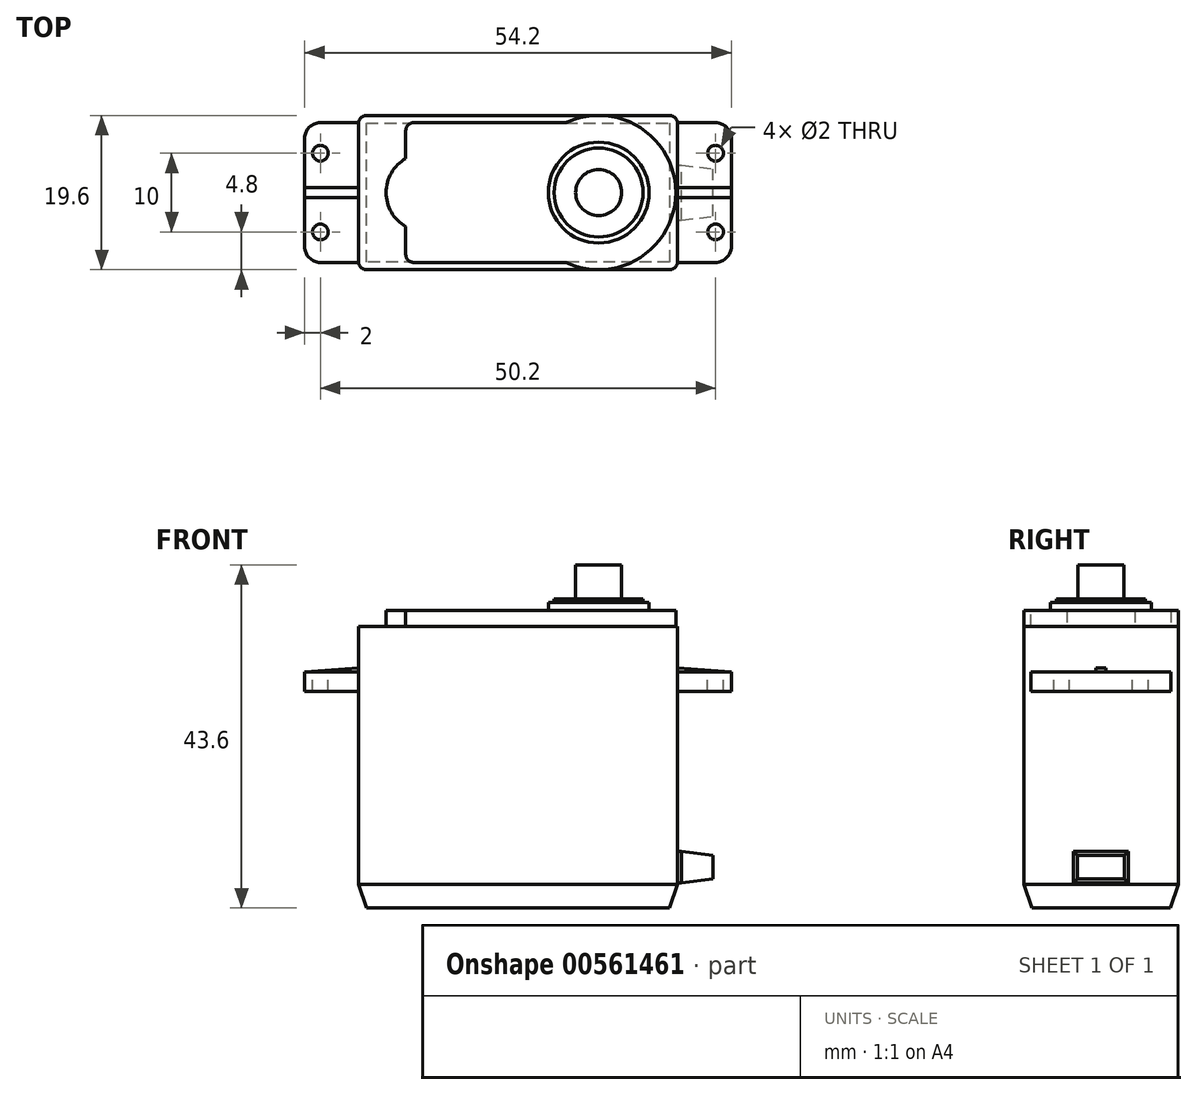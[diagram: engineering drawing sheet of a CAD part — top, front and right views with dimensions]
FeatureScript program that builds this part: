
annotation { "Feature Type Name" : "Feature", "Feature Type Description" : "" }
export const myFeature = defineFeature(function(context is Context, id is Id, definition is map)
    precondition{}
    {
        {
            var Q0;
            Q0=qCreatedBy(makeId("Front.planeOp"),FACE);
            var sketch = newSketch(context, id + "F0", { "sketchPlane" : qUnion([Q0])});
            skLineSegment(sketch, "E0.bottom", {"start": v(-20.25, 17.9) * mm, "end": v(20.25, 17.9) * mm});
            skLineSegment(sketch, "E0.top", {"start": v(-20.25, -17.9) * mm, "end": v(20.25, -17.9) * mm});
            skLineSegment(sketch, "E0.left", {"start": v(-20.25, 17.9) * mm, "end": v(-20.25, -17.9) * mm});
            skLineSegment(sketch, "E0.right", {"start": v(20.25, 17.9) * mm, "end": v(20.25, -17.9) * mm});
            skLineSegment(sketch, "E1.bottom", {"start": v(-27.1, 12.1) * mm, "end": v(27.1, 12.1) * mm});
            skLineSegment(sketch, "E1.top", {"start": v(-27.1, 9.6) * mm, "end": v(27.1, 9.6) * mm});
            skLineSegment(sketch, "E1.left", {"start": v(-27.1, 12.1) * mm, "end": v(-27.1, 9.6) * mm});
            skLineSegment(sketch, "E1.right", {"start": v(27.1, 12.1) * mm, "end": v(27.1, 9.6) * mm});
            skLineSegment(sketch, "E2", {"start": v(20.25, -10.7) * mm, "end": v(24.75, -10.7) * mm});
            skLineSegment(sketch, "E3", {"start": v(24.75, -10.7) * mm, "end": v(24.75, -14.7) * mm});
            skLineSegment(sketch, "E4", {"start": v(24.75, -14.7) * mm, "end": v(20.25, -14.7) * mm});
            skLineSegment(sketch, "E5", {"start": v(-27.1, 12.1) * mm, "end": v(-20.25, 12.6) * mm});
            skLineSegment(sketch, "E6", {"start": v(27.1, 12.1) * mm, "end": v(20.25, 12.6) * mm});
            skSolve(sketch);
        }
        {
            var Q0;
            {var subQ0=sQuery(id+"F0.wireOp",EDGE,"E0.bottom");Q0=makeQuery(id+"F0.imprint","IMPRINT",FACE,{"disambiguationData":[TD([[makeQuery(id+"F0.imprint","IMPRINT",EDGE,{"derivedFrom":subQ0}),-1.0]])]});}
            var Q1;
            {var subQ6=sQuery(id+"F0.wireOp",EDGE,"E0.top");Q1=makeQuery(id+"F0.imprint","IMPRINT",FACE,{"disambiguationData":[TD([[makeQuery(id+"F0.imprint","IMPRINT",EDGE,{"derivedFrom":subQ6}),1.0]])]});}
            var Q2;
            {var subQ0=sQuery(id+"F0.wireOp",EDGE,"E1.bottom");var subQ1=sQuery(id+"F0.wireOp",EDGE,"E0.left");var subQ2=makeQuery(id+"F0.imprint","INTERSECT",VERTEX,{"derivedFrom":[subQ1,subQ0]});Q2=makeQuery(id+"F0.imprint","IMPRINT",FACE,{"disambiguationData":[TD([[makeQuery(id+"F0.imprint","IMPRINT",EDGE,{"disambiguationData":[TD([[subQ2,-1.0]])],"derivedFrom":subQ1}),1.0]])]});}
            extrude(context, id + "F1", {"entities" : qUnion([Q0, Q1, Q2]), "depth" : 19.6 * mm, "offsetDistance" : 25 * mm, "symmetric" : true});
        }
        {
            var Q0;
            {var subQ5=sQuery(id+"F0.wireOp",EDGE,"E1.right");Q0=makeQuery(id+"F0.imprint","IMPRINT",FACE,{"disambiguationData":[TD([[makeQuery(id+"F0.imprint","IMPRINT",EDGE,{"derivedFrom":subQ5}),-1.0]])]});}
            var Q1;
            {var subQ5=sQuery(id+"F0.wireOp",EDGE,"E1.left");Q1=makeQuery(id+"F0.imprint","IMPRINT",FACE,{"disambiguationData":[TD([[makeQuery(id+"F0.imprint","IMPRINT",EDGE,{"derivedFrom":subQ5}),1.0]])]});}
            extrude(context, id + "F2", {"entities" : qUnion([Q0, Q1]), "operationType" : NewBodyOperationType.ADD, "depth" : 17.75 * mm, "offsetDistance" : 25 * mm, "symmetric" : true});
        }
        {
            var Q0;
            {var subQ0=sQuery(id+"F0.wireOp",EDGE,"E2");Q0=makeQuery(id+"F0.imprint","IMPRINT",FACE,{"disambiguationData":[TD([[makeQuery(id+"F0.imprint","IMPRINT",EDGE,{"derivedFrom":subQ0}),-1.0]])]});}
            extrude(context, id + "F3", {"entities" : qUnion([Q0]), "operationType" : NewBodyOperationType.ADD, "depth" : 7 * mm, "offsetDistance" : 25 * mm, "symmetric" : true});
        }
        {
            var Q0;
            Q0=makeQuery(id+"F3.opExtrude","SWEPT_EDGE",EDGE,{"disambiguationData":[OSD([sQuery(id+"F0.wireOp",EDGE,"E2"),sQuery(id+"F0.wireOp",EDGE,"E3")])]});
            var Q1;
            Q1=makeQuery(id+"F3.opExtrude","CAP_EDGE",EDGE,{"disambiguationData":[OSD([sQuery(id+"F0.wireOp",EDGE,"E3")])],"isStart":true});
            var Q2;
            Q2=makeQuery(id+"F3.opExtrude","CAP_EDGE",EDGE,{"disambiguationData":[OSD([sQuery(id+"F0.wireOp",EDGE,"E3")])],"isStart":false});
            var Q3;
            Q3=makeQuery(id+"F3.opExtrude","SWEPT_EDGE",EDGE,{"disambiguationData":[OSD([sQuery(id+"F0.wireOp",EDGE,"E3"),sQuery(id+"F0.wireOp",EDGE,"E4")])]});
            chamfer(context, id + "F4", {"entities" : qUnion([Q0, Q1, Q2, Q3]), "chamferType" : ChamferType.TWO_OFFSETS, "width1" : 4 * mm, "oppositeDirection" : false, "width2" : 0.5 * mm, "tangentPropagation" : true});
        }
        {
            var Q0;
            Q0=makeQuery(id+"F1.opExtrude","SWEPT_FACE",FACE,{"disambiguationData":[OSD([sQuery(id+"F0.wireOp",EDGE,"E0.bottom")])]});
            var sketch = newSketch(context, id + "F5", { "sketchPlane" : qUnion([Q0])});
            skCircle(sketch, "E7", {"center": v(10.25, 0) * mm, "radius": 9.8 * mm});
            skCircle(sketch, "E8", {"center": v(10.25, 0) * mm, "radius": 6.4 * mm});
            skCircle(sketch, "E9", {"center": v(10.25, 0) * mm, "radius": 5.65 * mm});
            skLineSegment(sketch, "E10.bottom", {"start": v(-14.25, 8.87) * mm, "end": v(10.75, 8.88) * mm});
            skLineSegment(sketch, "E10.top", {"start": v(-14.25, -8.88) * mm, "end": v(10.75, -8.87) * mm});
            skLineSegment(sketch, "E10.left", {"start": v(-14.25, 8.87) * mm, "end": v(-14.25, -8.88) * mm});
            skLineSegment(sketch, "E10.right", {"start": v(10.75, 8.88) * mm, "end": v(10.75, -8.87) * mm});
            skCircle(sketch, "E11", {"center": v(10.25, 0) * mm, "radius": 2.93 * mm});
            skCircle(sketch, "E12", {"center": v(-11.75, 0) * mm, "radius": 5 * mm});
            skSolve(sketch);
        }
        {
            var Q0;
            {var subQ0=sQuery(id+"F5.wireOp",EDGE,"E7");var subQ10=sQuery(id+"F5.wireOp",EDGE,"E10.bottom");var subQ11=makeQuery(id+"F5.imprint","INTERSECT",VERTEX,{"derivedFrom":[subQ0,subQ10]});Q0=makeQuery(id+"F5.imprint","IMPRINT",FACE,{"disambiguationData":[TD([[makeQuery(id+"F5.imprint","IMPRINT",EDGE,{"disambiguationData":[TD([[subQ11,1.0]])],"derivedFrom":subQ0}),1.0]])]});}
            var Q1;
            {var subQ0=sQuery(id+"F5.wireOp",EDGE,"E10.right");var subQ1=sQuery(id+"F5.wireOp",EDGE,"E8");var subQ2=makeQuery(id+"F5.imprint","INTERSECT",VERTEX,{"disambiguationData":[OD(0.0)],"derivedFrom":[subQ1,subQ0]});Q1=makeQuery(id+"F5.imprint","IMPRINT",FACE,{"disambiguationData":[TD([[makeQuery(id+"F5.imprint","IMPRINT",EDGE,{"disambiguationData":[TD([[subQ2,1.0]])],"derivedFrom":subQ1}),1.0]])]});}
            var Q2;
            {var subQ0=sQuery(id+"F5.wireOp",EDGE,"E10.right");var subQ1=sQuery(id+"F5.wireOp",EDGE,"E9");var subQ2=makeQuery(id+"F5.imprint","INTERSECT",VERTEX,{"disambiguationData":[OD(0.0)],"derivedFrom":[subQ1,subQ0]});Q2=makeQuery(id+"F5.imprint","IMPRINT",FACE,{"disambiguationData":[TD([[makeQuery(id+"F5.imprint","IMPRINT",EDGE,{"disambiguationData":[TD([[subQ2,1.0]])],"derivedFrom":subQ1}),1.0]])]});}
            var Q3;
            {var subQ0=sQuery(id+"F5.wireOp",EDGE,"E10.right");var subQ1=sQuery(id+"F5.wireOp",EDGE,"E9");var subQ2=makeQuery(id+"F5.imprint","INTERSECT",VERTEX,{"disambiguationData":[OD(0.0)],"derivedFrom":[subQ1,subQ0]});Q3=makeQuery(id+"F5.imprint","IMPRINT",FACE,{"disambiguationData":[TD([[makeQuery(id+"F5.imprint","IMPRINT",EDGE,{"disambiguationData":[TD([[subQ2,-1.0]])],"derivedFrom":subQ1}),1.0]])]});}
            var Q4;
            {var subQ0=sQuery(id+"F5.wireOp",EDGE,"E11");var subQ1=sQuery(id+"F5.wireOp",EDGE,"E10.right");var subQ2=makeQuery(id+"F5.imprint","INTERSECT",VERTEX,{"disambiguationData":[OD(0.0)],"derivedFrom":[subQ1,subQ0]});Q4=makeQuery(id+"F5.imprint","IMPRINT",FACE,{"disambiguationData":[TD([[makeQuery(id+"F5.imprint","IMPRINT",EDGE,{"disambiguationData":[TD([[subQ2,-1.0]])],"derivedFrom":subQ1}),-1.0]])]});}
            var Q5;
            {var subQ0=sQuery(id+"F5.wireOp",EDGE,"E11");var subQ1=sQuery(id+"F5.wireOp",EDGE,"E10.right");var subQ2=makeQuery(id+"F5.imprint","INTERSECT",VERTEX,{"disambiguationData":[OD(0.0)],"derivedFrom":[subQ1,subQ0]});Q5=makeQuery(id+"F5.imprint","IMPRINT",FACE,{"disambiguationData":[TD([[makeQuery(id+"F5.imprint","IMPRINT",EDGE,{"disambiguationData":[TD([[subQ2,-1.0]])],"derivedFrom":subQ1}),1.0]])]});}
            var Q6;
            {var subQ0=sQuery(id+"F5.wireOp",EDGE,"E10.right");var subQ1=sQuery(id+"F5.wireOp",EDGE,"E8");var subQ2=makeQuery(id+"F5.imprint","INTERSECT",VERTEX,{"disambiguationData":[OD(0.0)],"derivedFrom":[subQ1,subQ0]});Q6=makeQuery(id+"F5.imprint","IMPRINT",FACE,{"disambiguationData":[TD([[makeQuery(id+"F5.imprint","IMPRINT",EDGE,{"disambiguationData":[TD([[subQ2,-1.0]])],"derivedFrom":subQ1}),1.0]])]});}
            var Q7;
            {var subQ1=sQuery(id+"F5.wireOp",EDGE,"E10.bottom");var subQ3=sQuery(id+"F5.wireOp",EDGE,"E7");var subQ4=makeQuery(id+"F5.imprint","INTERSECT",VERTEX,{"derivedFrom":[subQ3,subQ1]});Q7=makeQuery(id+"F5.imprint","IMPRINT",FACE,{"disambiguationData":[TD([[makeQuery(id+"F5.imprint","IMPRINT",EDGE,{"disambiguationData":[TD([[subQ4,-1.0]])],"derivedFrom":subQ3}),1.0]])]});}
            var Q8;
            {var subQ1=sQuery(id+"F5.wireOp",EDGE,"E10.bottom");var subQ5=sQuery(id+"F5.wireOp",EDGE,"E7");var subQ6=makeQuery(id+"F5.imprint","INTERSECT",VERTEX,{"derivedFrom":[subQ5,subQ1]});Q8=makeQuery(id+"F5.imprint","IMPRINT",FACE,{"disambiguationData":[TD([[makeQuery(id+"F5.imprint","IMPRINT",EDGE,{"disambiguationData":[TD([[subQ6,-1.0]])],"derivedFrom":subQ5}),-1.0]])]});}
            var Q9;
            {var subQ0=sQuery(id+"F5.wireOp",EDGE,"E12");var subQ1=sQuery(id+"F5.wireOp",EDGE,"E10.left");var subQ2=makeQuery(id+"F5.imprint","INTERSECT",VERTEX,{"disambiguationData":[OD(0.0)],"derivedFrom":[subQ1,subQ0]});Q9=makeQuery(id+"F5.imprint","IMPRINT",FACE,{"disambiguationData":[TD([[makeQuery(id+"F5.imprint","IMPRINT",EDGE,{"disambiguationData":[TD([[subQ2,-1.0]])],"derivedFrom":subQ1}),1.0]])]});}
            var Q10;
            {var subQ0=sQuery(id+"F5.wireOp",EDGE,"E12");var subQ1=sQuery(id+"F5.wireOp",EDGE,"E10.left");var subQ2=makeQuery(id+"F5.imprint","INTERSECT",VERTEX,{"disambiguationData":[OD(0.0)],"derivedFrom":[subQ1,subQ0]});Q10=makeQuery(id+"F5.imprint","IMPRINT",FACE,{"disambiguationData":[TD([[makeQuery(id+"F5.imprint","IMPRINT",EDGE,{"disambiguationData":[TD([[subQ2,-1.0]])],"derivedFrom":subQ1}),-1.0]])]});}
            extrude(context, id + "F6", {"entities" : qUnion([Q0, Q1, Q2, Q3, Q4, Q5, Q6, Q7, Q8, Q9, Q10]), "operationType" : NewBodyOperationType.ADD, "depth" : 2 * mm, "offsetDistance" : 25 * mm});
        }
        {
            var Q0;
            {var subQ0=sQuery(id+"F5.wireOp",EDGE,"E10.right");var subQ1=sQuery(id+"F5.wireOp",EDGE,"E9");var subQ2=makeQuery(id+"F5.imprint","INTERSECT",VERTEX,{"disambiguationData":[OD(0.0)],"derivedFrom":[subQ1,subQ0]});Q0=makeQuery(id+"F5.imprint","IMPRINT",FACE,{"disambiguationData":[TD([[makeQuery(id+"F5.imprint","IMPRINT",EDGE,{"disambiguationData":[TD([[subQ2,-1.0]])],"derivedFrom":subQ1}),1.0]])]});}
            var Q1;
            {var subQ0=sQuery(id+"F5.wireOp",EDGE,"E11");var subQ1=sQuery(id+"F5.wireOp",EDGE,"E10.right");var subQ2=makeQuery(id+"F5.imprint","INTERSECT",VERTEX,{"disambiguationData":[OD(0.0)],"derivedFrom":[subQ1,subQ0]});Q1=makeQuery(id+"F5.imprint","IMPRINT",FACE,{"disambiguationData":[TD([[makeQuery(id+"F5.imprint","IMPRINT",EDGE,{"disambiguationData":[TD([[subQ2,-1.0]])],"derivedFrom":subQ1}),-1.0]])]});}
            var Q2;
            {var subQ0=sQuery(id+"F5.wireOp",EDGE,"E11");var subQ1=sQuery(id+"F5.wireOp",EDGE,"E10.right");var subQ2=makeQuery(id+"F5.imprint","INTERSECT",VERTEX,{"disambiguationData":[OD(0.0)],"derivedFrom":[subQ1,subQ0]});Q2=makeQuery(id+"F5.imprint","IMPRINT",FACE,{"disambiguationData":[TD([[makeQuery(id+"F5.imprint","IMPRINT",EDGE,{"disambiguationData":[TD([[subQ2,-1.0]])],"derivedFrom":subQ1}),1.0]])]});}
            var Q3;
            {var subQ0=sQuery(id+"F5.wireOp",EDGE,"E10.right");var subQ1=sQuery(id+"F5.wireOp",EDGE,"E9");var subQ2=makeQuery(id+"F5.imprint","INTERSECT",VERTEX,{"disambiguationData":[OD(0.0)],"derivedFrom":[subQ1,subQ0]});Q3=makeQuery(id+"F5.imprint","IMPRINT",FACE,{"disambiguationData":[TD([[makeQuery(id+"F5.imprint","IMPRINT",EDGE,{"disambiguationData":[TD([[subQ2,1.0]])],"derivedFrom":subQ1}),1.0]])]});}
            var Q4;
            {var subQ0=sQuery(id+"F5.wireOp",EDGE,"E10.right");var subQ1=sQuery(id+"F5.wireOp",EDGE,"E8");var subQ2=makeQuery(id+"F5.imprint","INTERSECT",VERTEX,{"disambiguationData":[OD(0.0)],"derivedFrom":[subQ1,subQ0]});Q4=makeQuery(id+"F5.imprint","IMPRINT",FACE,{"disambiguationData":[TD([[makeQuery(id+"F5.imprint","IMPRINT",EDGE,{"disambiguationData":[TD([[subQ2,1.0]])],"derivedFrom":subQ1}),1.0]])]});}
            var Q5;
            {var subQ0=sQuery(id+"F5.wireOp",EDGE,"E10.right");var subQ1=sQuery(id+"F5.wireOp",EDGE,"E8");var subQ2=makeQuery(id+"F5.imprint","INTERSECT",VERTEX,{"disambiguationData":[OD(0.0)],"derivedFrom":[subQ1,subQ0]});Q5=makeQuery(id+"F5.imprint","IMPRINT",FACE,{"disambiguationData":[TD([[makeQuery(id+"F5.imprint","IMPRINT",EDGE,{"disambiguationData":[TD([[subQ2,-1.0]])],"derivedFrom":subQ1}),1.0]])]});}
            extrude(context, id + "F7", {"entities" : qUnion([Q0, Q1, Q2, Q3, Q4, Q5]), "operationType" : NewBodyOperationType.ADD, "depth" : 3 * mm, "offsetDistance" : 25 * mm});
        }
        {
            var Q0;
            {var subQ0=sQuery(id+"F5.wireOp",EDGE,"E11");var subQ1=sQuery(id+"F5.wireOp",EDGE,"E10.right");var subQ2=makeQuery(id+"F5.imprint","INTERSECT",VERTEX,{"disambiguationData":[OD(0.0)],"derivedFrom":[subQ1,subQ0]});Q0=makeQuery(id+"F5.imprint","IMPRINT",FACE,{"disambiguationData":[TD([[makeQuery(id+"F5.imprint","IMPRINT",EDGE,{"disambiguationData":[TD([[subQ2,-1.0]])],"derivedFrom":subQ1}),1.0]])]});}
            var Q1;
            {var subQ0=sQuery(id+"F5.wireOp",EDGE,"E11");var subQ1=sQuery(id+"F5.wireOp",EDGE,"E10.right");var subQ2=makeQuery(id+"F5.imprint","INTERSECT",VERTEX,{"disambiguationData":[OD(0.0)],"derivedFrom":[subQ1,subQ0]});Q1=makeQuery(id+"F5.imprint","IMPRINT",FACE,{"disambiguationData":[TD([[makeQuery(id+"F5.imprint","IMPRINT",EDGE,{"disambiguationData":[TD([[subQ2,-1.0]])],"derivedFrom":subQ1}),-1.0]])]});}
            var Q2;
            {var subQ0=sQuery(id+"F5.wireOp",EDGE,"E10.right");var subQ1=sQuery(id+"F5.wireOp",EDGE,"E9");var subQ2=makeQuery(id+"F5.imprint","INTERSECT",VERTEX,{"disambiguationData":[OD(0.0)],"derivedFrom":[subQ1,subQ0]});Q2=makeQuery(id+"F5.imprint","IMPRINT",FACE,{"disambiguationData":[TD([[makeQuery(id+"F5.imprint","IMPRINT",EDGE,{"disambiguationData":[TD([[subQ2,-1.0]])],"derivedFrom":subQ1}),1.0]])]});}
            var Q3;
            {var subQ0=sQuery(id+"F5.wireOp",EDGE,"E10.right");var subQ1=sQuery(id+"F5.wireOp",EDGE,"E9");var subQ2=makeQuery(id+"F5.imprint","INTERSECT",VERTEX,{"disambiguationData":[OD(0.0)],"derivedFrom":[subQ1,subQ0]});Q3=makeQuery(id+"F5.imprint","IMPRINT",FACE,{"disambiguationData":[TD([[makeQuery(id+"F5.imprint","IMPRINT",EDGE,{"disambiguationData":[TD([[subQ2,1.0]])],"derivedFrom":subQ1}),1.0]])]});}
            extrude(context, id + "F8", {"entities" : qUnion([Q0, Q1, Q2, Q3]), "operationType" : NewBodyOperationType.ADD, "depth" : 3.5 * mm, "offsetDistance" : 25 * mm});
        }
        {
            var Q0;
            {var subQ0=sQuery(id+"F5.wireOp",EDGE,"E11");var subQ1=sQuery(id+"F5.wireOp",EDGE,"E10.right");var subQ2=makeQuery(id+"F5.imprint","INTERSECT",VERTEX,{"disambiguationData":[OD(0.0)],"derivedFrom":[subQ1,subQ0]});Q0=makeQuery(id+"F5.imprint","IMPRINT",FACE,{"disambiguationData":[TD([[makeQuery(id+"F5.imprint","IMPRINT",EDGE,{"disambiguationData":[TD([[subQ2,-1.0]])],"derivedFrom":subQ1}),-1.0]])]});}
            var Q1;
            {var subQ0=sQuery(id+"F5.wireOp",EDGE,"E11");var subQ1=sQuery(id+"F5.wireOp",EDGE,"E10.right");var subQ2=makeQuery(id+"F5.imprint","INTERSECT",VERTEX,{"disambiguationData":[OD(0.0)],"derivedFrom":[subQ1,subQ0]});Q1=makeQuery(id+"F5.imprint","IMPRINT",FACE,{"disambiguationData":[TD([[makeQuery(id+"F5.imprint","IMPRINT",EDGE,{"disambiguationData":[TD([[subQ2,-1.0]])],"derivedFrom":subQ1}),1.0]])]});}
            extrude(context, id + "F9", {"entities" : qUnion([Q0, Q1]), "operationType" : NewBodyOperationType.ADD, "depth" : 7.8 * mm, "offsetDistance" : 25 * mm});
        }
        {
            var Q0;
            {var subQ0=sQuery(id+"F0.wireOp",EDGE,"E6");Q0=makeQuery(id+"F0.imprint","IMPRINT",FACE,{"disambiguationData":[TD([[makeQuery(id+"F0.imprint","IMPRINT",EDGE,{"derivedFrom":subQ0}),1.0]])]});}
            var Q1;
            {var subQ0=sQuery(id+"F0.wireOp",EDGE,"E5");Q1=makeQuery(id+"F0.imprint","IMPRINT",FACE,{"disambiguationData":[TD([[makeQuery(id+"F0.imprint","IMPRINT",EDGE,{"derivedFrom":subQ0}),-1.0]])]});}
            extrude(context, id + "F10", {"entities" : qUnion([Q0, Q1]), "operationType" : NewBodyOperationType.ADD, "depth" : 1.3 * mm, "offsetDistance" : 25 * mm, "symmetric" : true});
        }
        {
            var Q0;
            {var subQ1=sQuery(id+"F0.wireOp",EDGE,"E6");var subQ2=sQuery(id+"F0.wireOp",EDGE,"E1.bottom");var subQ3=sQuery(id+"F0.wireOp",EDGE,"E0.right");Q0=makeQuery(id+"F10.boolean.opBoolean","SPLIT",FACE,{"disambiguationData":[TD([makeQuery(id+"F10.opExtrude","CAP_FACE",FACE,{"disambiguationData":[OSD([subQ3,subQ2,subQ1])],"isStart":true})])],"derivedFrom":makeQuery(id+"F2.opExtrude","SWEPT_FACE",FACE,{"disambiguationData":[OSD([subQ2]),TDD([makeQuery(id+"F0.imprint","IMPRINT",EDGE,{"disambiguationData":[TD([[makeQuery(id+"F0.imprint","INTERSECT",VERTEX,{"derivedFrom":[subQ3,subQ2]}),-1.0]])],"derivedFrom":subQ2})])]})});}
            var sketch = newSketch(context, id + "F11", { "sketchPlane" : qUnion([Q0])});
            skCircle(sketch, "E13", {"center": v(25.1, 5) * mm, "radius": 1 * mm});
            skPoint(sketch, "E13.centerSnap0", {"position": v(21.57, 5) * mm});
            skCircle(sketch, "E14", {"center": v(25.1, -5) * mm, "radius": 1 * mm});
            skCircle(sketch, "E15", {"center": v(-25.1, 5) * mm, "radius": 1 * mm});
            skCircle(sketch, "E16", {"center": v(-25.1, -5) * mm, "radius": 1 * mm});
            skSolve(sketch);
        }
        {
            var Q0;
            Q0=makeQuery(id+"F11.imprint","IMPRINT",FACE,{"disambiguationData":[TD([[makeQuery(id+"F11.imprint","IMPRINT",EDGE,{"derivedFrom":sQuery(id+"F11.wireOp",EDGE,"E15")}),1.0]])]});
            var Q1;
            Q1=makeQuery(id+"F11.imprint","IMPRINT",FACE,{"disambiguationData":[TD([[makeQuery(id+"F11.imprint","IMPRINT",EDGE,{"derivedFrom":sQuery(id+"F11.wireOp",EDGE,"E16")}),1.0]])]});
            var Q2;
            Q2=makeQuery(id+"F11.imprint","IMPRINT",FACE,{"disambiguationData":[TD([[makeQuery(id+"F11.imprint","IMPRINT",EDGE,{"derivedFrom":sQuery(id+"F11.wireOp",EDGE,"E13")}),1.0]])]});
            var Q3;
            Q3=makeQuery(id+"F11.imprint","IMPRINT",FACE,{"disambiguationData":[TD([[makeQuery(id+"F11.imprint","IMPRINT",EDGE,{"derivedFrom":sQuery(id+"F11.wireOp",EDGE,"E14")}),1.0]])]});
            extrude(context, id + "F12", {"entities" : qUnion([Q0, Q1, Q2, Q3]), "operationType" : NewBodyOperationType.REMOVE, "oppositeDirection" : true, "depth" : 5 * mm, "offsetDistance" : 25 * mm});
        }
        {
            var Q0;
            Q0=makeQuery(id+"F2.opExtrude","CAP_EDGE",EDGE,{"disambiguationData":[OSD([sQuery(id+"F0.wireOp",EDGE,"E1.right")])],"isStart":false});
            var Q1;
            Q1=makeQuery(id+"F2.opExtrude","CAP_EDGE",EDGE,{"disambiguationData":[OSD([sQuery(id+"F0.wireOp",EDGE,"E1.right")])],"isStart":true});
            var Q2;
            Q2=makeQuery(id+"F2.opExtrude","CAP_EDGE",EDGE,{"disambiguationData":[OSD([sQuery(id+"F0.wireOp",EDGE,"E1.left")])],"isStart":false});
            var Q3;
            Q3=makeQuery(id+"F2.opExtrude","CAP_EDGE",EDGE,{"disambiguationData":[OSD([sQuery(id+"F0.wireOp",EDGE,"E1.left")])],"isStart":true});
            fillet(context, id + "F13", {"entities" : qUnion([Q0, Q1, Q2, Q3]), "radius" : 2 * mm, "tangentPropagation" : true, "allowEdgeOverflow" : false});
        }
        {
            var Q0;
            Q0=makeQuery(id+"F6.opExtrude","SWEPT_EDGE",EDGE,{"disambiguationData":[OSD([sQuery(id+"F5.wireOp",EDGE,"E10.top"),sQuery(id+"F5.wireOp",EDGE,"E10.left")])]});
            var Q1;
            Q1=makeQuery(id+"F6.opExtrude","SWEPT_EDGE",EDGE,{"disambiguationData":[OSD([sQuery(id+"F5.wireOp",EDGE,"E10.bottom"),sQuery(id+"F5.wireOp",EDGE,"E10.left")])]});
            var Q2;
            Q2=makeQuery(id+"F6.opExtrude","SWEPT_EDGE",EDGE,{"disambiguationData":[OSD([sQuery(id+"F5.wireOp",EDGE,"E7"),sQuery(id+"F5.wireOp",EDGE,"E10.bottom")])]});
            var Q3;
            Q3=makeQuery(id+"F6.opExtrude","SWEPT_EDGE",EDGE,{"disambiguationData":[OSD([sQuery(id+"F5.wireOp",EDGE,"E7"),sQuery(id+"F5.wireOp",EDGE,"E10.top")])]});
            fillet(context, id + "F14", {"entities" : qUnion([Q0, Q1, Q2, Q3]), "radius" : 1 * mm, "tangentPropagation" : true, "allowEdgeOverflow" : false});
        }
        {
            var Q0;
            Q0=makeQuery(id+"F1.opExtrude","CAP_EDGE",EDGE,{"disambiguationData":[OSD([sQuery(id+"F0.wireOp",EDGE,"E0.right")])],"isStart":false});
            var Q1;
            Q1=makeQuery(id+"F1.opExtrude","CAP_EDGE",EDGE,{"disambiguationData":[OSD([sQuery(id+"F0.wireOp",EDGE,"E0.left")])],"isStart":false});
            var Q2;
            Q2=makeQuery(id+"F1.opExtrude","CAP_EDGE",EDGE,{"disambiguationData":[OSD([sQuery(id+"F0.wireOp",EDGE,"E0.left")])],"isStart":true});
            var Q3;
            Q3=makeQuery(id+"F1.opExtrude","CAP_EDGE",EDGE,{"disambiguationData":[OSD([sQuery(id+"F0.wireOp",EDGE,"E0.right")])],"isStart":true});
            fillet(context, id + "F15", {"entities" : qUnion([Q0, Q1, Q2, Q3]), "radius" : 1 * mm, "tangentPropagation" : true, "allowEdgeOverflow" : false});
        }
        {
            var Q0;
            Q0=makeQuery(id+"F1.opExtrude","CAP_EDGE",EDGE,{"disambiguationData":[OSD([sQuery(id+"F0.wireOp",EDGE,"E0.top")])],"isStart":false});
            var Q1;
            Q1=makeQuery(id+"F1.opExtrude","SWEPT_EDGE",EDGE,{"disambiguationData":[OSD([sQuery(id+"F0.wireOp",EDGE,"E0.top"),sQuery(id+"F0.wireOp",EDGE,"E0.right")])]});
            var Q2;
            Q2=makeQuery(id+"F1.opExtrude","CAP_EDGE",EDGE,{"disambiguationData":[OSD([sQuery(id+"F0.wireOp",EDGE,"E0.top")])],"isStart":true});
            var Q3;
            Q3=makeQuery(id+"F1.opExtrude","SWEPT_EDGE",EDGE,{"disambiguationData":[OSD([sQuery(id+"F0.wireOp",EDGE,"E0.top"),sQuery(id+"F0.wireOp",EDGE,"E0.left")])]});
            chamfer(context, id + "F16", {"entities" : qUnion([Q0, Q1, Q2, Q3]), "chamferType" : ChamferType.TWO_OFFSETS, "width1" : 3 * mm, "oppositeDirection" : false, "width2" : 1 * mm, "tangentPropagation" : true});
        }
    });
